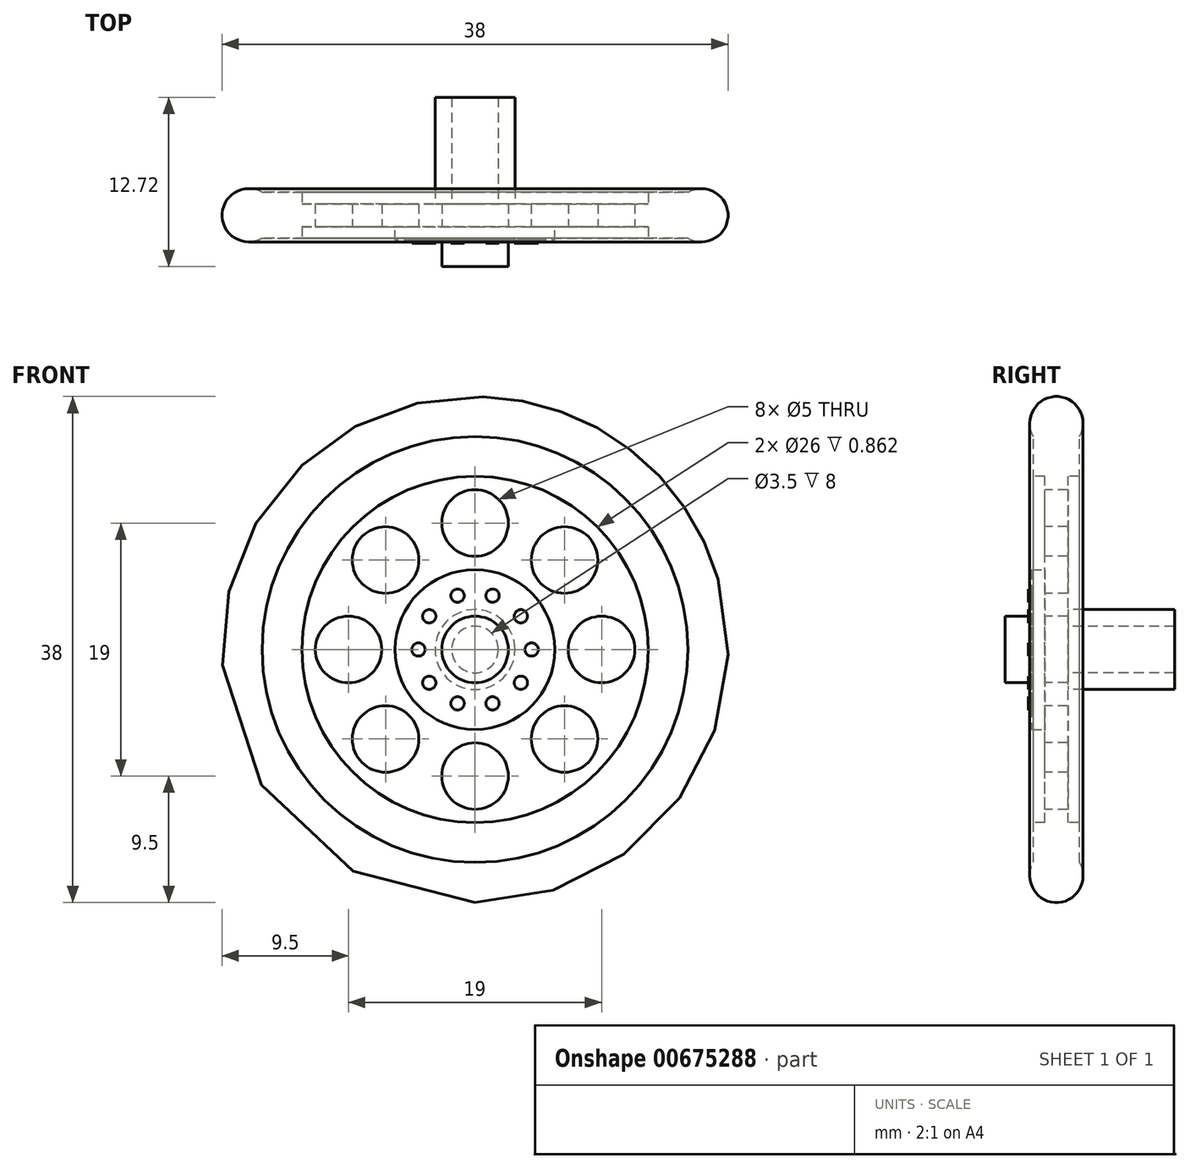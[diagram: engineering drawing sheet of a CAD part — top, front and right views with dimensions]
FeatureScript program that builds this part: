
annotation { "Feature Type Name" : "Feature", "Feature Type Description" : "" }
export const myFeature = defineFeature(function(context is Context, id is Id, definition is map)
    precondition{}
    {
        {
            var Q0;
            Q0=qCreatedBy(makeId("Right.planeOp"),FACE);
            var sketch = newSketch(context, id + "F0", { "sketchPlane" : qUnion([Q0])});
            skPoint(sketch, "E0", {"position": v(0, 0) * mm});
            skArc(sketch, "E1", {"start": v(1.72, 15.98) * mm, "mid": v(0, 19) * mm, "end": v(-1.72, 15.98) * mm});
            skLineSegment(sketch, "E2", {"start": v(-1.72, 15.98) * mm, "end": v(-1.72, 13) * mm});
            skLineSegment(sketch, "E3.MirrorCS", {"start": v(1.72, 15.98) * mm, "end": v(1.72, 13) * mm});
            skPoint(sketch, "E4", {"position": v(0.86, 13) * mm});
            skLineSegment(sketch, "E5", {"start": v(0.86, 13) * mm, "end": v(1.72, 13) * mm});
            skLineSegment(sketch, "E6.MirrorCS", {"start": v(-0.86, 13) * mm, "end": v(-1.72, 13) * mm});
            skLineSegment(sketch, "E7", {"start": v(-0.86, 13) * mm, "end": v(-0.86, 0) * mm});
            skLineSegment(sketch, "E8", {"start": v(0.86, 13) * mm, "end": v(0.86, 0) * mm});
            skLineSegment(sketch, "E9", {"start": v(-0.86, 0) * mm, "end": v(0.86, 0) * mm});
            skSolve(sketch);
        }
        {
            var Q0;
            Q0=makeQuery(id+"F0.imprint","IMPRINT",FACE,{"disambiguationData":[TD([[makeQuery(id+"F0.imprint","IMPRINT",EDGE,{"derivedFrom":sQuery(id+"F0.wireOp",EDGE,"E1")}),1.0]])]});
            var Q1;
            Q1=sQuery(id+"F0.wireOp",EDGE,"E9");
            revolve(context, id + "F1", {"entities" : qUnion([Q0]), "axis" : qUnion([Q1]), "revolveType" : RevolveType.FULL});
        }
        {
            var Q0;
            Q0=makeQuery(id+"F1.opRevolve","SWEPT_FACE",FACE,{"disambiguationData":[OSD([sQuery(id+"F0.wireOp",EDGE,"E7")])]});
            var sketch = newSketch(context, id + "F2", { "sketchPlane" : qUnion([Q0])});
            skCircle(sketch, "E10", {"center": v(0, 0) * mm, "radius": 2.5 * mm});
            skCircle(sketch, "E11", {"center": v(0, 0) * mm, "radius": 6 * mm});
            skPoint(sketch, "E12", {"position": v(9.5, 0) * mm});
            skCircle(sketch, "E13", {"center": v(9.5, 0) * mm, "radius": 2.5 * mm});
            skPoint(sketch, "E14", {"position": v(4.25, 0) * mm});
            skCircle(sketch, "E15", {"center": v(4.25, 0) * mm, "radius": 0.5 * mm});
            skCircle(sketch, "E16.1.0", {"center": v(6.72, -6.72) * mm, "radius": 2.5 * mm});
            skCircle(sketch, "E16.2.0", {"center": v(0, -9.5) * mm, "radius": 2.5 * mm});
            skLineSegment(sketch, "E16.anchor1", {"start": v(0, 0) * mm, "end": v(9.5, 0) * mm, "construction": true});
            skLineSegment(sketch, "E16.anchor2", {"start": v(0, 0) * mm, "end": v(0, -9.5) * mm, "construction": true});
            skCircle(sketch, "E17.1.0", {"center": v(-6.72, -6.72) * mm, "radius": 2.5 * mm});
            skCircle(sketch, "E17.2.0", {"center": v(-9.5, 0) * mm, "radius": 2.5 * mm});
            skLineSegment(sketch, "E17.anchor2", {"start": v(0, 0) * mm, "end": v(-9.5, 0) * mm, "construction": true});
            skCircle(sketch, "E18.1.0", {"center": v(-6.72, 6.72) * mm, "radius": 2.5 * mm});
            skCircle(sketch, "E18.2.0", {"center": v(0, 9.5) * mm, "radius": 2.5 * mm});
            skLineSegment(sketch, "E18.anchor2", {"start": v(0, 0) * mm, "end": v(0, 9.5) * mm, "construction": true});
            skCircle(sketch, "E19.1.0", {"center": v(6.72, 6.72) * mm, "radius": 2.5 * mm});
            skCircle(sketch, "E20.1.0", {"center": v(3.44, 2.5) * mm, "radius": 0.5 * mm});
            skCircle(sketch, "E20.2.0", {"center": v(1.31, 4.04) * mm, "radius": 0.5 * mm});
            skCircle(sketch, "E20.3.0", {"center": v(-1.31, 4.04) * mm, "radius": 0.5 * mm});
            skCircle(sketch, "E20.4.0", {"center": v(-3.44, 2.5) * mm, "radius": 0.5 * mm});
            skCircle(sketch, "E20.5.0", {"center": v(-4.25, 0) * mm, "radius": 0.5 * mm});
            skCircle(sketch, "E20.6.0", {"center": v(-3.44, -2.5) * mm, "radius": 0.5 * mm});
            skCircle(sketch, "E20.7.0", {"center": v(-1.31, -4.04) * mm, "radius": 0.5 * mm});
            skCircle(sketch, "E20.8.0", {"center": v(1.31, -4.04) * mm, "radius": 0.5 * mm});
            skCircle(sketch, "E20.9.0", {"center": v(3.44, -2.5) * mm, "radius": 0.5 * mm});
            skSolve(sketch);
        }
        {
            var Q0;
            Q0=makeQuery(id+"F2.imprint","IMPRINT",FACE,{"disambiguationData":[TD([[makeQuery(id+"F2.imprint","IMPRINT",EDGE,{"derivedFrom":sQuery(id+"F2.wireOp",EDGE,"E18.2.0")}),1.0]])]});
            var Q1;
            Q1=makeQuery(id+"F2.imprint","IMPRINT",FACE,{"disambiguationData":[TD([[makeQuery(id+"F2.imprint","IMPRINT",EDGE,{"derivedFrom":sQuery(id+"F2.wireOp",EDGE,"E19.1.0")}),1.0]])]});
            var Q2;
            Q2=makeQuery(id+"F2.imprint","IMPRINT",FACE,{"disambiguationData":[TD([[makeQuery(id+"F2.imprint","IMPRINT",EDGE,{"derivedFrom":sQuery(id+"F2.wireOp",EDGE,"E13")}),1.0]])]});
            var Q3;
            Q3=makeQuery(id+"F2.imprint","IMPRINT",FACE,{"disambiguationData":[TD([[makeQuery(id+"F2.imprint","IMPRINT",EDGE,{"derivedFrom":sQuery(id+"F2.wireOp",EDGE,"E16.1.0")}),1.0]])]});
            var Q4;
            Q4=makeQuery(id+"F2.imprint","IMPRINT",FACE,{"disambiguationData":[TD([[makeQuery(id+"F2.imprint","IMPRINT",EDGE,{"derivedFrom":sQuery(id+"F2.wireOp",EDGE,"E16.2.0")}),1.0]])]});
            var Q5;
            Q5=makeQuery(id+"F2.imprint","IMPRINT",FACE,{"disambiguationData":[TD([[makeQuery(id+"F2.imprint","IMPRINT",EDGE,{"derivedFrom":sQuery(id+"F2.wireOp",EDGE,"E17.1.0")}),1.0]])]});
            var Q6;
            Q6=makeQuery(id+"F2.imprint","IMPRINT",FACE,{"disambiguationData":[TD([[makeQuery(id+"F2.imprint","IMPRINT",EDGE,{"derivedFrom":sQuery(id+"F2.wireOp",EDGE,"E17.2.0")}),1.0]])]});
            var Q7;
            Q7=makeQuery(id+"F2.imprint","IMPRINT",FACE,{"disambiguationData":[TD([[makeQuery(id+"F2.imprint","IMPRINT",EDGE,{"derivedFrom":sQuery(id+"F2.wireOp",EDGE,"E18.1.0")}),1.0]])]});
            extrude(context, id + "F3", {"entities" : qUnion([Q0, Q1, Q2, Q3, Q4, Q5, Q6, Q7]), "operationType" : NewBodyOperationType.REMOVE, "oppositeDirection" : true, "depth" : 25.4 * mm, "offsetDistance" : 25.4 * mm});
        }
        {
            var Q0;
            Q0=makeQuery(id+"F2.imprint","IMPRINT",FACE,{"disambiguationData":[TD([[makeQuery(id+"F2.imprint","IMPRINT",EDGE,{"derivedFrom":sQuery(id+"F2.wireOp",EDGE,"E10")}),1.0]])]});
            extrude(context, id + "F4", {"entities" : qUnion([Q0]), "operationType" : NewBodyOperationType.ADD, "depth" : 3 * mm, "offsetDistance" : 25.4 * mm});
        }
        {
            var Q0;
            Q0=makeQuery(id+"F2.imprint","IMPRINT",FACE,{"disambiguationData":[TD([[makeQuery(id+"F2.imprint","IMPRINT",EDGE,{"derivedFrom":sQuery(id+"F2.wireOp",EDGE,"E10")}),-1.0]])]});
            extrude(context, id + "F5", {"entities" : qUnion([Q0]), "operationType" : NewBodyOperationType.ADD, "depth" : 1 * mm, "offsetDistance" : 25.4 * mm});
        }
        {
            var Q0;
            Q0=makeQuery(id+"F2.imprint","IMPRINT",FACE,{"disambiguationData":[TD([[makeQuery(id+"F2.imprint","IMPRINT",EDGE,{"derivedFrom":sQuery(id+"F2.wireOp",EDGE,"E20.3.0")}),1.0]])]});
            var Q1;
            Q1=makeQuery(id+"F2.imprint","IMPRINT",FACE,{"disambiguationData":[TD([[makeQuery(id+"F2.imprint","IMPRINT",EDGE,{"derivedFrom":sQuery(id+"F2.wireOp",EDGE,"E20.2.0")}),1.0]])]});
            var Q2;
            Q2=makeQuery(id+"F2.imprint","IMPRINT",FACE,{"disambiguationData":[TD([[makeQuery(id+"F2.imprint","IMPRINT",EDGE,{"derivedFrom":sQuery(id+"F2.wireOp",EDGE,"E20.1.0")}),1.0]])]});
            var Q3;
            Q3=makeQuery(id+"F2.imprint","IMPRINT",FACE,{"disambiguationData":[TD([[makeQuery(id+"F2.imprint","IMPRINT",EDGE,{"derivedFrom":sQuery(id+"F2.wireOp",EDGE,"E15")}),1.0]])]});
            var Q4;
            Q4=makeQuery(id+"F2.imprint","IMPRINT",FACE,{"disambiguationData":[TD([[makeQuery(id+"F2.imprint","IMPRINT",EDGE,{"derivedFrom":sQuery(id+"F2.wireOp",EDGE,"E20.9.0")}),1.0]])]});
            var Q5;
            Q5=makeQuery(id+"F2.imprint","IMPRINT",FACE,{"disambiguationData":[TD([[makeQuery(id+"F2.imprint","IMPRINT",EDGE,{"derivedFrom":sQuery(id+"F2.wireOp",EDGE,"E20.8.0")}),1.0]])]});
            var Q6;
            Q6=makeQuery(id+"F2.imprint","IMPRINT",FACE,{"disambiguationData":[TD([[makeQuery(id+"F2.imprint","IMPRINT",EDGE,{"derivedFrom":sQuery(id+"F2.wireOp",EDGE,"E20.7.0")}),1.0]])]});
            var Q7;
            Q7=makeQuery(id+"F2.imprint","IMPRINT",FACE,{"disambiguationData":[TD([[makeQuery(id+"F2.imprint","IMPRINT",EDGE,{"derivedFrom":sQuery(id+"F2.wireOp",EDGE,"E20.6.0")}),1.0]])]});
            var Q8;
            Q8=makeQuery(id+"F2.imprint","IMPRINT",FACE,{"disambiguationData":[TD([[makeQuery(id+"F2.imprint","IMPRINT",EDGE,{"derivedFrom":sQuery(id+"F2.wireOp",EDGE,"E20.5.0")}),1.0]])]});
            var Q9;
            Q9=makeQuery(id+"F2.imprint","IMPRINT",FACE,{"disambiguationData":[TD([[makeQuery(id+"F2.imprint","IMPRINT",EDGE,{"derivedFrom":sQuery(id+"F2.wireOp",EDGE,"E20.4.0")}),1.0]])]});
            extrude(context, id + "F6", {"entities" : qUnion([Q0, Q1, Q2, Q3, Q4, Q5, Q6, Q7, Q8, Q9]), "operationType" : NewBodyOperationType.ADD, "depth" : 1.25 * mm, "offsetDistance" : 25.4 * mm});
        }
        {
            var Q0;
            Q0=makeQuery(id+"F1.opRevolve","SWEPT_FACE",FACE,{"disambiguationData":[OSD([sQuery(id+"F0.wireOp",EDGE,"E8")])]});
            var sketch = newSketch(context, id + "F7", { "sketchPlane" : qUnion([Q0])});
            skCircle(sketch, "E21", {"center": v(0, 0) * mm, "radius": 3 * mm});
            skCircle(sketch, "E22", {"center": v(0, 0) * mm, "radius": 1.75 * mm});
            skSolve(sketch);
        }
        {
            var Q0;
            Q0=makeQuery(id+"F7.imprint","IMPRINT",FACE,{"disambiguationData":[TD([[makeQuery(id+"F7.imprint","IMPRINT",EDGE,{"derivedFrom":sQuery(id+"F7.wireOp",EDGE,"E21")}),1.0]])]});
            extrude(context, id + "F8", {"entities" : qUnion([Q0]), "operationType" : NewBodyOperationType.ADD, "depth" : 8 * mm, "offsetDistance" : 25.4 * mm});
        }
    });
